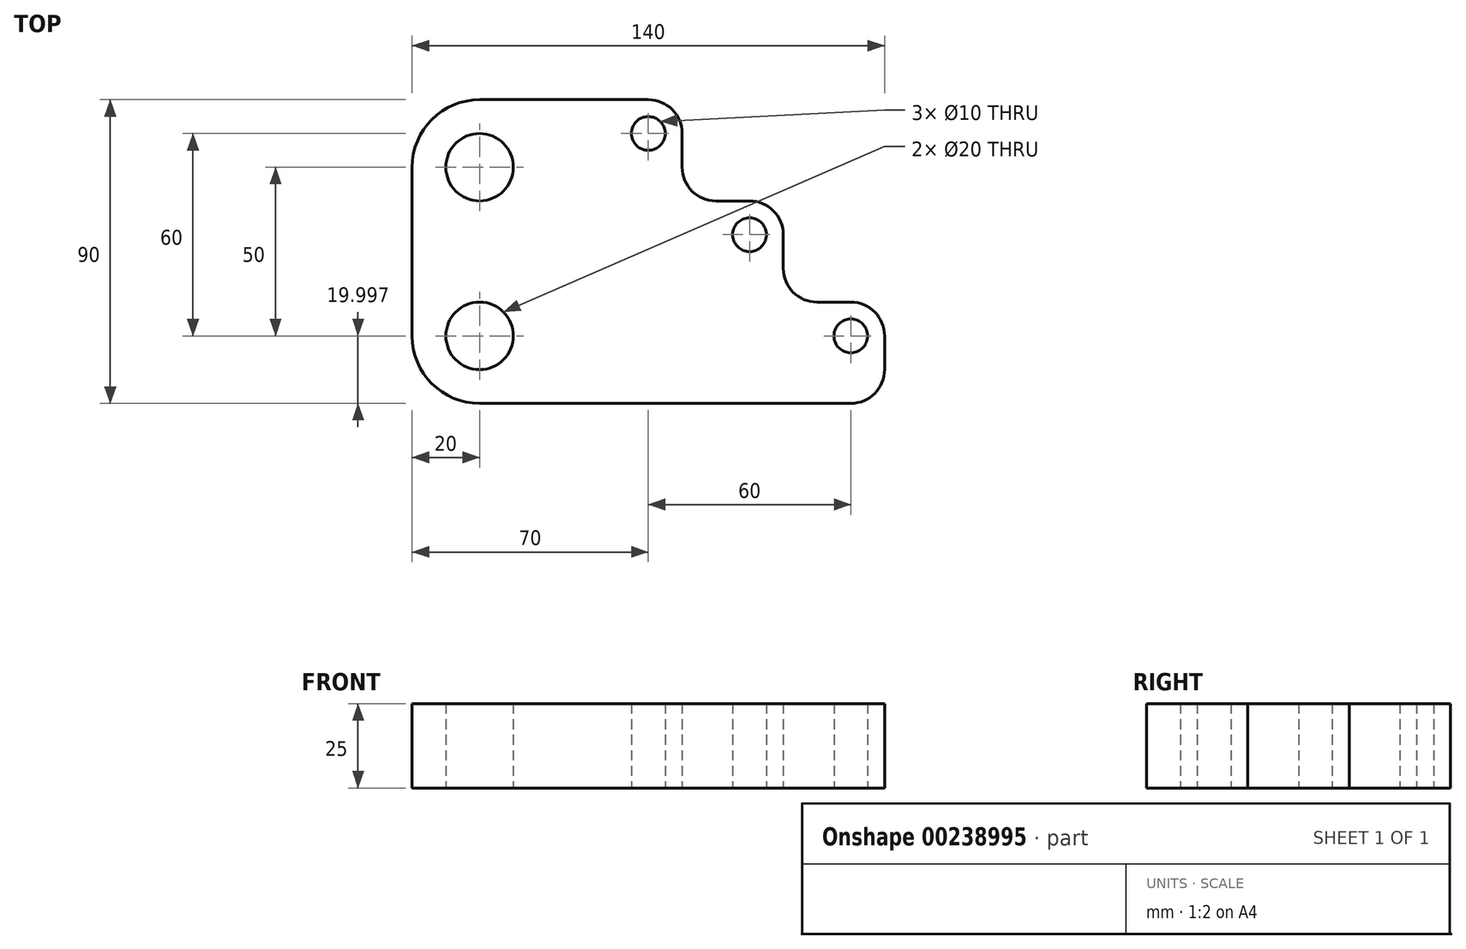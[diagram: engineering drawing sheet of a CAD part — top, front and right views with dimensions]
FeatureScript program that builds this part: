
annotation { "Feature Type Name" : "Feature", "Feature Type Description" : "" }
export const myFeature = defineFeature(function(context is Context, id is Id, definition is map)
    precondition{}
    {
        {
            var Q0;
            Q0=qCreatedBy(makeId("Top.planeOp"),FACE);
            var sketch = newSketch(context, id + "F0", { "sketchPlane" : qUnion([Q0])});
            skLineSegment(sketch, "E0", {"start": v(-60, 23.43) * mm, "end": v(50, 23.43) * mm});
            skLineSegment(sketch, "E1", {"start": v(-80, 43.43) * mm, "end": v(-80, 93.43) * mm});
            skLineSegment(sketch, "E2", {"start": v(-60, 113.43) * mm, "end": v(-10, 113.43) * mm});
            skLineSegment(sketch, "E3", {"start": v(60, 33.43) * mm, "end": v(60, 43.43) * mm});
            skLineSegment(sketch, "E4", {"start": v(50, 53.43) * mm, "end": v(40, 53.43) * mm});
            skLineSegment(sketch, "E5", {"start": v(30, 63.43) * mm, "end": v(30, 73.43) * mm});
            skLineSegment(sketch, "E6", {"start": v(20, 83.43) * mm, "end": v(10, 83.43) * mm});
            skLineSegment(sketch, "E7", {"start": v(0, 103.43) * mm, "end": v(0, 93.43) * mm});
            skCircle(sketch, "E8", {"center": v(-60, 43.43) * mm, "radius": 10 * mm});
            skCircle(sketch, "E9", {"center": v(-60, 93.43) * mm, "radius": 10 * mm});
            skCircle(sketch, "E10", {"center": v(50, 43.43) * mm, "radius": 5 * mm});
            skCircle(sketch, "E11", {"center": v(20, 73.43) * mm, "radius": 5 * mm});
            skCircle(sketch, "E12", {"center": v(-10, 103.43) * mm, "radius": 5 * mm});
            skPoint(sketch, "E13.visualSharp", {"position": v(60, 53.43) * mm});
            skArc(sketch, "E13.filletArc", {"start": v(60, 43.43) * mm, "mid": v(57.07, 50.5) * mm, "end": v(50, 53.43) * mm});
            skPoint(sketch, "E14.visualSharp", {"position": v(30, 83.43) * mm});
            skArc(sketch, "E14.filletArc", {"start": v(30, 73.43) * mm, "mid": v(27.07, 80.5) * mm, "end": v(20, 83.43) * mm});
            skPoint(sketch, "E15.visualSharp", {"position": v(0, 113.43) * mm});
            skArc(sketch, "E15.filletArc", {"start": v(0, 103.43) * mm, "mid": v(-2.93, 110.5) * mm, "end": v(-10, 113.43) * mm});
            skPoint(sketch, "E16.visualSharp", {"position": v(-80, 113.43) * mm});
            skArc(sketch, "E16.filletArc", {"start": v(-60, 113.43) * mm, "mid": v(-74.14, 107.57) * mm, "end": v(-80, 93.43) * mm});
            skPoint(sketch, "E17.visualSharp", {"position": v(-80, 23.43) * mm});
            skArc(sketch, "E17.filletArc", {"start": v(-80, 43.43) * mm, "mid": v(-74.14, 29.29) * mm, "end": v(-60, 23.43) * mm});
            skPoint(sketch, "E18.visualSharp", {"position": v(0, 83.43) * mm});
            skArc(sketch, "E18.filletArc", {"start": v(0, 93.43) * mm, "mid": v(2.93, 86.36) * mm, "end": v(10, 83.43) * mm});
            skPoint(sketch, "E19.visualSharp", {"position": v(30, 53.43) * mm});
            skArc(sketch, "E19.filletArc", {"start": v(30, 63.43) * mm, "mid": v(32.93, 56.36) * mm, "end": v(40, 53.43) * mm});
            skPoint(sketch, "E20.visualSharp", {"position": v(60, 23.43) * mm});
            skArc(sketch, "E20.filletArc", {"start": v(50, 23.43) * mm, "mid": v(57.07, 26.36) * mm, "end": v(60, 33.43) * mm});
            skSolve(sketch);
        }
        {
            var Q0;
            Q0=makeQuery(id+"F0.imprint","IMPRINT",FACE,{"disambiguationData":[TD([[makeQuery(id+"F0.imprint","IMPRINT",EDGE,{"derivedFrom":sQuery(id+"F0.wireOp",EDGE,"E0")}),1.0]])]});
            extrude(context, id + "F1", {"entities" : qUnion([Q0]), "depth" : 25 * mm});
        }
    });
